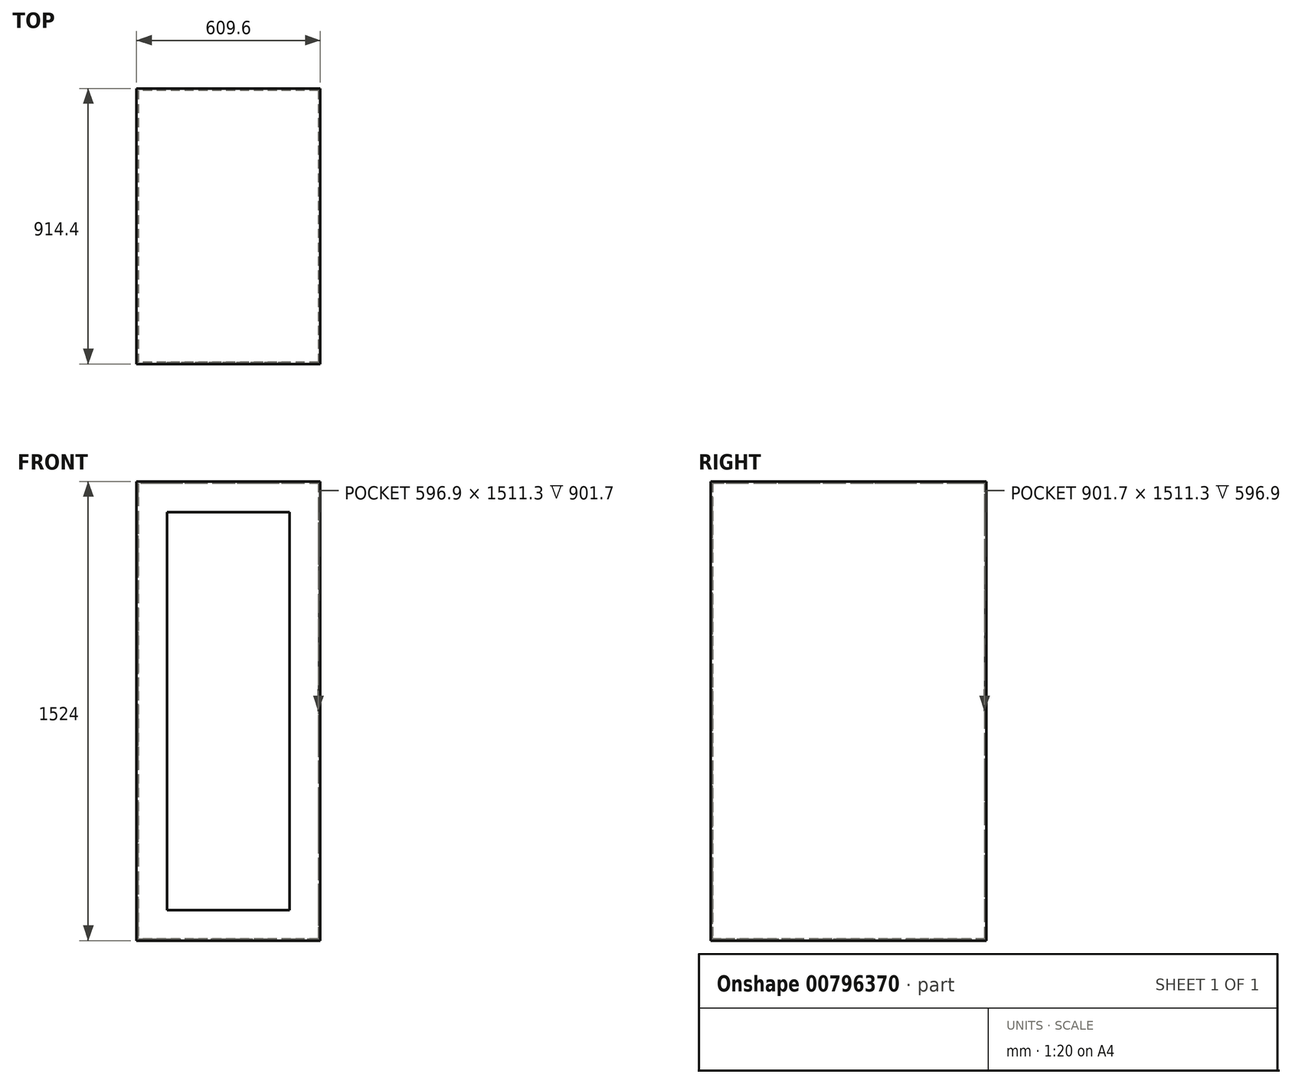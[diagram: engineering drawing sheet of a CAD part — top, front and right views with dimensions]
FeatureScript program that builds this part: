
annotation { "Feature Type Name" : "Feature", "Feature Type Description" : "" }
export const myFeature = defineFeature(function(context is Context, id is Id, definition is map)
    precondition{}
    {
        {
            var Q0;
            Q0=qCreatedBy(makeId("Top.planeOp"),FACE);
            var sketch = newSketch(context, id + "F0", { "sketchPlane" : qUnion([Q0])});
            skLineSegment(sketch, "E0.bottom", {"start": v(0, 0) * mm, "end": v(-609.6, 0) * mm});
            skLineSegment(sketch, "E0.top", {"start": v(0, -914.4) * mm, "end": v(-609.6, -914.4) * mm});
            skLineSegment(sketch, "E0.left", {"start": v(0, 0) * mm, "end": v(0, -914.4) * mm});
            skLineSegment(sketch, "E0.right", {"start": v(-609.6, 0) * mm, "end": v(-609.6, -914.4) * mm});
            skSolve(sketch);
        }
        {
            var Q0;
            Q0 = qSketchRegion(id + "F0", true);
            extrude(context, id + "F1", {"entities" : qUnion([Q0]), "depth" : 1524 * mm, "offsetDistance" : 25.4 * mm});
        }
        {
            var Q0;
            Q0=makeQuery(id+"F1.opExtrude","SWEPT_FACE",FACE,{"disambiguationData":[OSD([sQuery(id+"F0.wireOp",EDGE,"E0.top")])]});
            shell(context, id + "F2", {"entities" : qUnion([Q0]), "thickness" : 6.35 * mm});
        }
        {
            var Q0;
            Q0=makeQuery(id+"F1.opExtrude","SWEPT_FACE",FACE,{"disambiguationData":[OSD([sQuery(id+"F0.wireOp",EDGE,"E0.top")])]});
            var sketch = newSketch(context, id + "F3", { "sketchPlane" : qUnion([Q0])});
            skLineSegment(sketch, "E1.bottom", {"start": v(0, 1524) * mm, "end": v(-609.6, 1524) * mm});
            skLineSegment(sketch, "E1.top", {"start": v(0, 0) * mm, "end": v(-609.6, 0) * mm});
            skLineSegment(sketch, "E1.left", {"start": v(0, 1524) * mm, "end": v(0, 0) * mm});
            skLineSegment(sketch, "E1.right", {"start": v(-609.6, 1524) * mm, "end": v(-609.6, 0) * mm});
            skLineSegment(sketch, "E2.bottom", {"start": v(-508, 1422.4) * mm, "end": v(-101.6, 1422.4) * mm});
            skLineSegment(sketch, "E2.top", {"start": v(-508, 101.6) * mm, "end": v(-101.6, 101.6) * mm});
            skLineSegment(sketch, "E2.left", {"start": v(-508, 1422.4) * mm, "end": v(-508, 101.6) * mm});
            skLineSegment(sketch, "E2.right", {"start": v(-101.6, 1422.4) * mm, "end": v(-101.6, 101.6) * mm});
            skSolve(sketch);
        }
        {
            var Q0;
            Q0=makeQuery(id+"F3.imprint","IMPRINT",FACE,{"disambiguationData":[TD([[makeQuery(id+"F3.imprint","IMPRINT",EDGE,{"derivedFrom":sQuery(id+"F3.wireOp",EDGE,"E2.bottom")}),1.0]])]});
            extrude(context, id + "F4", {"entities" : qUnion([Q0]), "operationType" : NewBodyOperationType.ADD, "oppositeDirection" : true, "depth" : 6.35 * mm, "offsetDistance" : 25.4 * mm});
        }
    });
